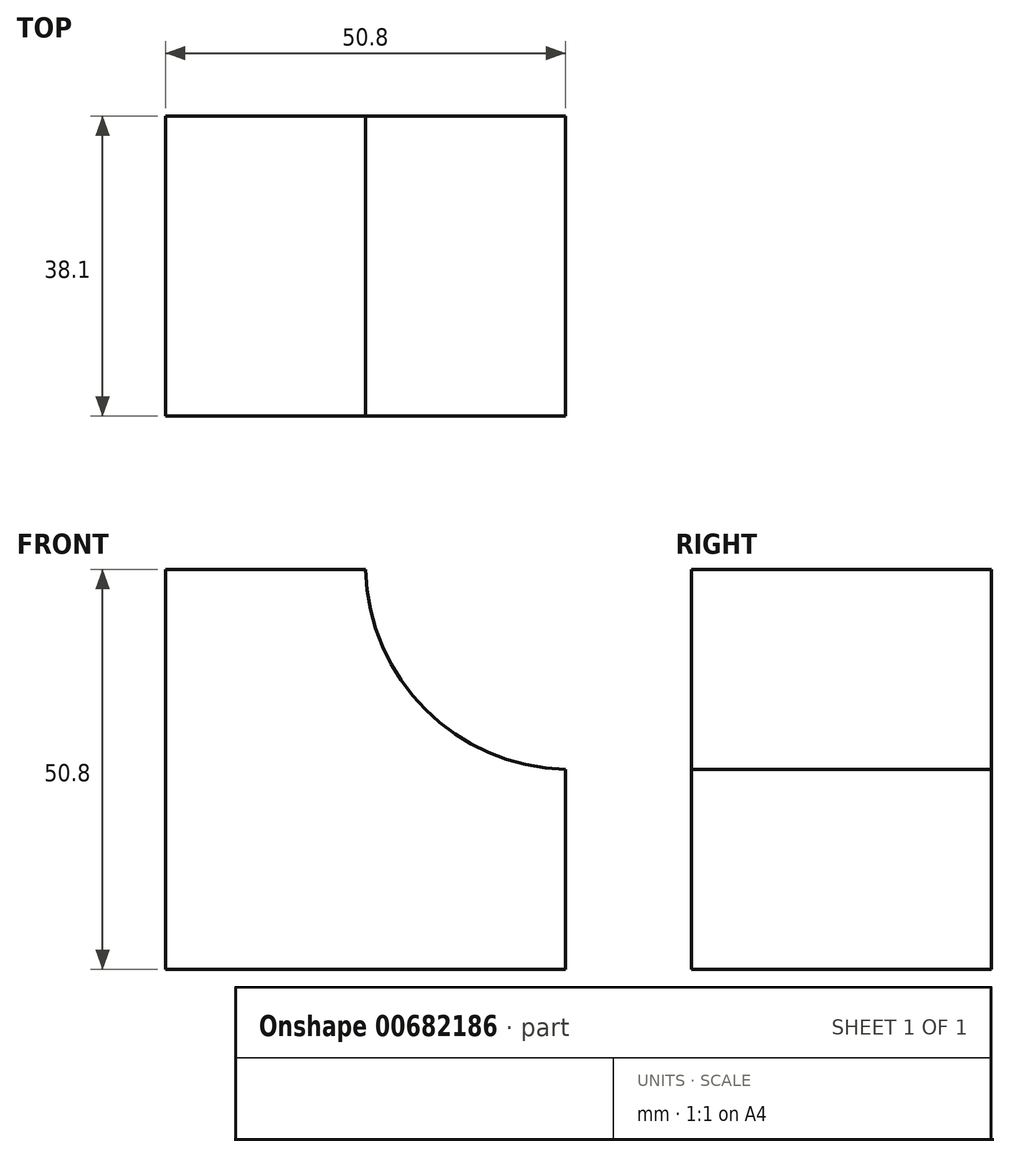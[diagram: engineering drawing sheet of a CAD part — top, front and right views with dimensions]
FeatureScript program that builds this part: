
annotation { "Feature Type Name" : "Feature", "Feature Type Description" : "" }
export const myFeature = defineFeature(function(context is Context, id is Id, definition is map)
    precondition{}
    {
        {
            var Q0;
            Q0=qCreatedBy(makeId("Front.planeOp"),FACE);
            var sketch = newSketch(context, id + "F0", { "sketchPlane" : qUnion([Q0])});
            skLineSegment(sketch, "E0", {"start": v(-39.77, 42.63) * mm, "end": v(-39.77, -8.17) * mm});
            skLineSegment(sketch, "E1", {"start": v(-39.77, -8.17) * mm, "end": v(11.03, -8.17) * mm});
            skLineSegment(sketch, "E2", {"start": v(11.03, -8.17) * mm, "end": v(11.03, 17.23) * mm});
            skLineSegment(sketch, "E3", {"start": v(-39.77, 42.63) * mm, "end": v(-14.37, 42.63) * mm});
            skArc(sketch, "E4", {"start": v(-14.37, 42.63) * mm, "mid": v(-6.75, 24.84) * mm, "end": v(11.03, 17.23) * mm});
            skSolve(sketch);
        }
        {
            var Q0;
            Q0=makeQuery(id+"F0.imprint","IMPRINT",FACE,{"disambiguationData":[TD([[makeQuery(id+"F0.imprint","IMPRINT",EDGE,{"derivedFrom":sQuery(id+"F0.wireOp",EDGE,"E0")}),1.0]])]});
            extrude(context, id + "F1", {"entities" : qUnion([Q0]), "depth" : 38.1 * mm, "offsetDistance" : 25.4 * mm});
        }
    });
